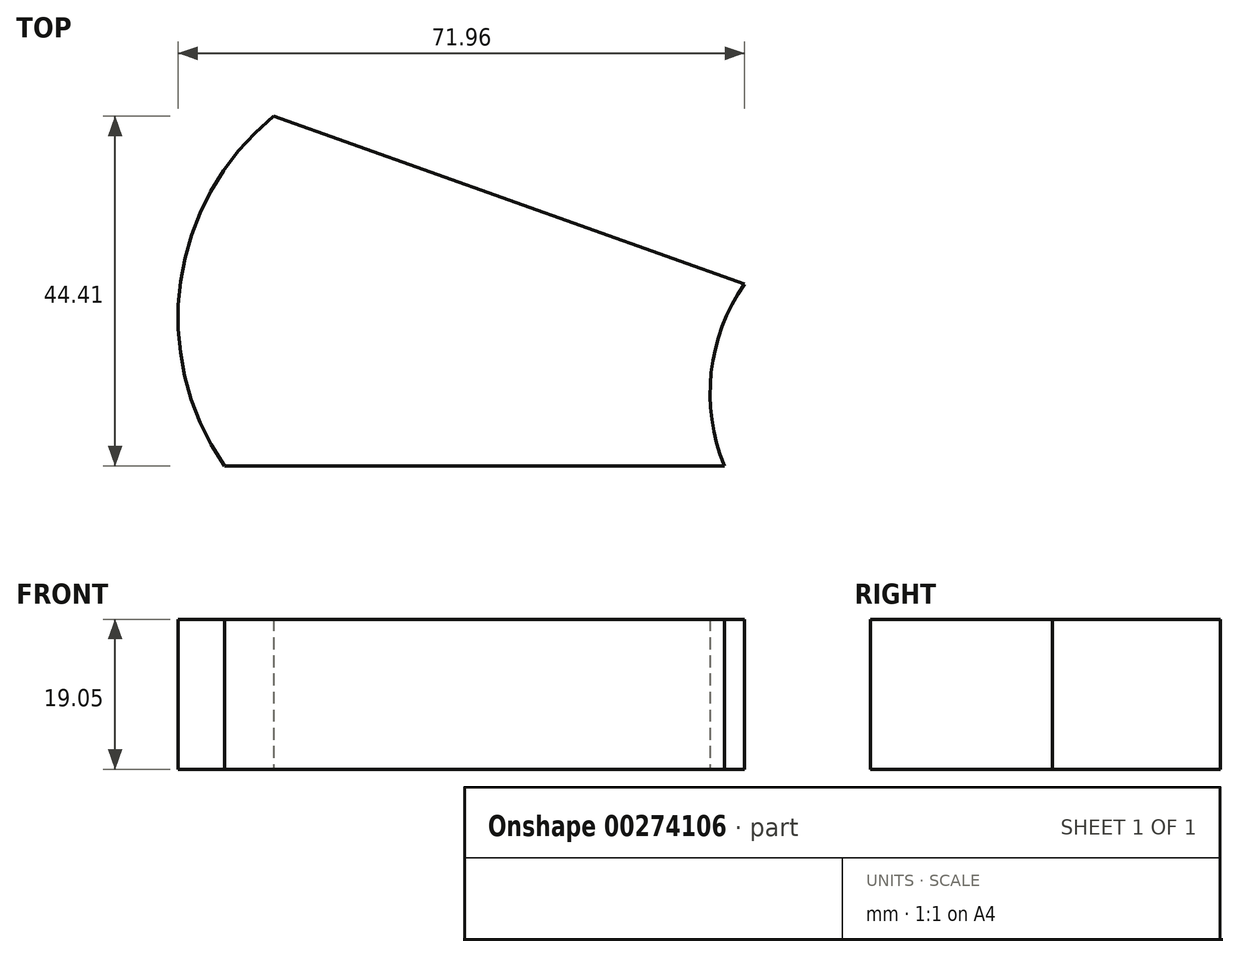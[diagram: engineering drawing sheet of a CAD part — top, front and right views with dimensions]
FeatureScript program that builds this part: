
annotation { "Feature Type Name" : "Feature", "Feature Type Description" : "" }
export const myFeature = defineFeature(function(context is Context, id is Id, definition is map)
    precondition{}
    {
        {
            var Q0;
            Q0=qCreatedBy(makeId("Top.planeOp"),FACE);
            var sketch = newSketch(context, id + "F0", { "sketchPlane" : qUnion([Q0])});
            skLineSegment(sketch, "E0", {"start": v(-34.98, -17.19) * mm, "end": v(28.52, -17.19) * mm});
            skLineSegment(sketch, "E1", {"start": v(-28.73, 27.22) * mm, "end": v(31.09, 5.92) * mm});
            skArc(sketch, "E2", {"start": v(31.09, 5.92) * mm, "mid": v(26.86, -5.3) * mm, "end": v(28.52, -17.19) * mm});
            skArc(sketch, "E3", {"start": v(-28.73, 27.22) * mm, "mid": v(-40.55, 6.24) * mm, "end": v(-34.98, -17.19) * mm});
            skSolve(sketch);
        }
        {
            var Q0;
            Q0 = qSketchRegion(id + "F0", true);
            extrude(context, id + "F1", {"entities" : qUnion([Q0]), "depth" : 19.05 * mm});
        }
    });
